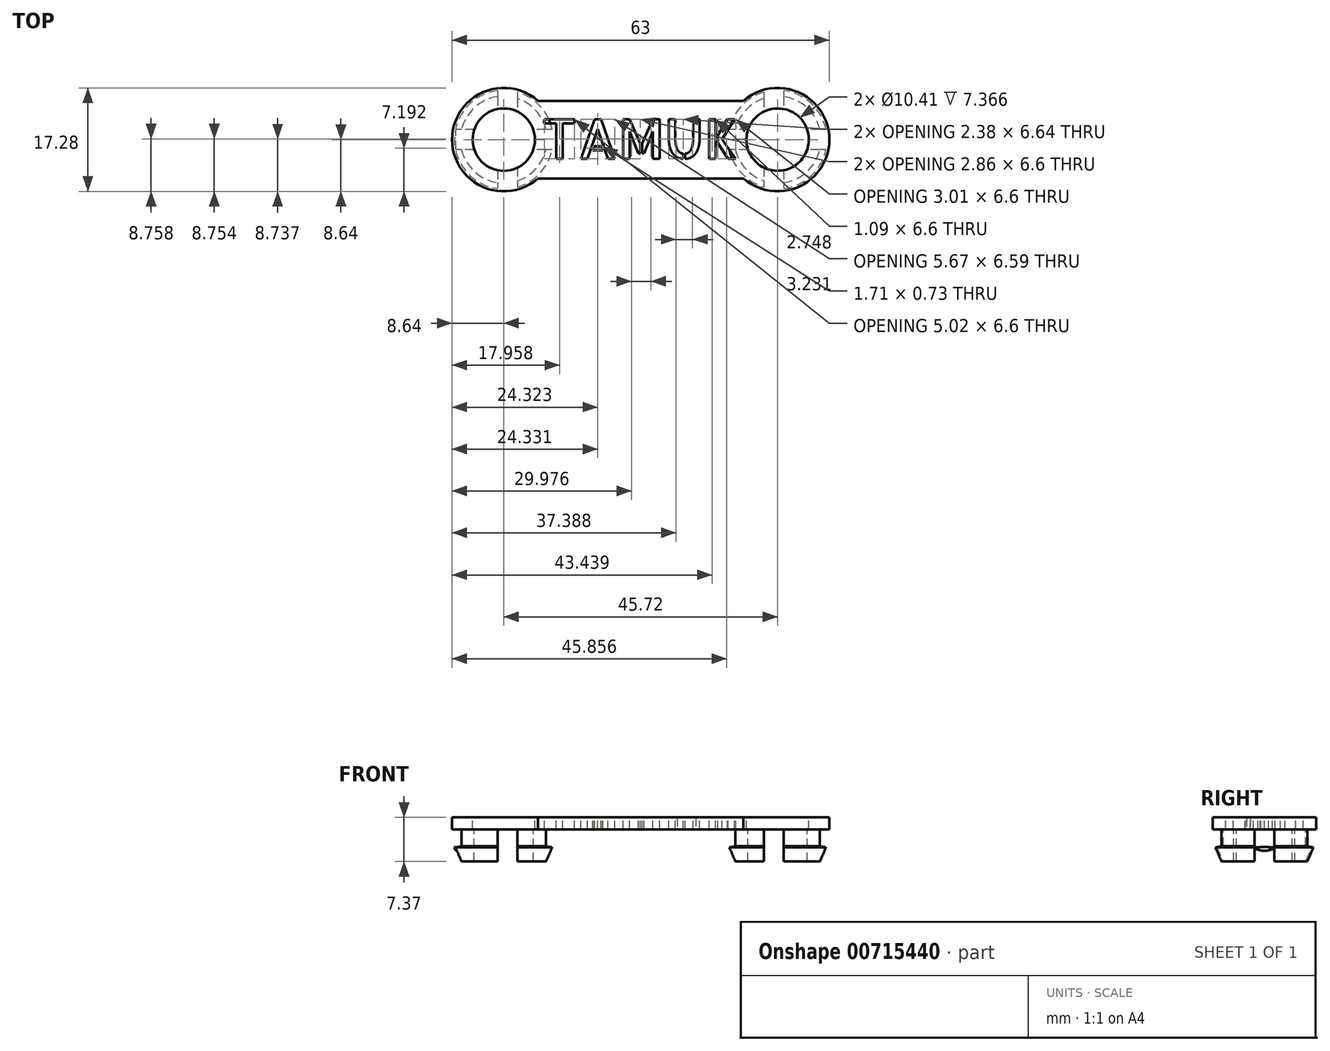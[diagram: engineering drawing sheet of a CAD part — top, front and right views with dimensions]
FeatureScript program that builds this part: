
annotation { "Feature Type Name" : "Feature", "Feature Type Description" : "" }
export const myFeature = defineFeature(function(context is Context, id is Id, definition is map)
    precondition{}
    {
        {
            var Q0;
            Q0=qCreatedBy(makeId("Top.planeOp"),FACE);
            var sketch = newSketch(context, id + "F0", { "sketchPlane" : qUnion([Q0])});
            skLineSegment(sketch, "E0", {"start": v(-17.15, -6.48) * mm, "end": v(17.15, -6.48) * mm});
            skLineSegment(sketch, "E1", {"start": v(-17.15, 6.48) * mm, "end": v(17.15, 6.48) * mm});
            skPoint(sketch, "E2", {"position": v(0, 6.48) * mm});
            skArc(sketch, "E3", {"start": v(-17.15, 6.48) * mm, "mid": v(-31.5, 0) * mm, "end": v(-17.15, -6.48) * mm});
            skArc(sketch, "E4", {"start": v(17.15, -6.48) * mm, "mid": v(31.5, 0) * mm, "end": v(17.15, 6.48) * mm});
            skSolve(sketch);
        }
        {
            var Q0;
            Q0=qCreatedBy(makeId("Front.planeOp"),FACE);
            var sketch = newSketch(context, id + "F1", { "sketchPlane" : qUnion([Q0])});
            skLineSegment(sketch, "E5", {"start": v(-28.07, 7.37) * mm, "end": v(-30.1, 7.37) * mm});
            skLineSegment(sketch, "E6", {"start": v(-30.1, 7.37) * mm, "end": v(-30.1, 7.37) * mm});
            skLineSegment(sketch, "E7", {"start": v(-30.1, 7.37) * mm, "end": v(-31.1, 5) * mm});
            skLineSegment(sketch, "E8", {"start": v(-31.1, 5) * mm, "end": v(-30.1, 4.83) * mm});
            skLineSegment(sketch, "E9", {"start": v(-22.86, 2.03) * mm, "end": v(-22.86, 0) * mm});
            skLineSegment(sketch, "E10", {"start": v(-28.07, 7.37) * mm, "end": v(-28.07, 2.03) * mm});
            skLineSegment(sketch, "E11", {"start": v(-30.1, 4.83) * mm, "end": v(-30.1, 2.03) * mm});
            skLineSegment(sketch, "E12", {"start": v(-28.07, 2.03) * mm, "end": v(-30.1, 2.03) * mm});
            skLineSegment(sketch, "E13", {"start": v(-22.86, 2.03) * mm, "end": v(-30.1, 2.03) * mm});
            skLineSegment(sketch, "E14.MirrorCS", {"start": v(-30.1, -7.37) * mm, "end": v(-31.1, -5) * mm});
            skLineSegment(sketch, "E15.MirrorCS", {"start": v(-30.1, -7.37) * mm, "end": v(-30.1, -7.37) * mm});
            skLineSegment(sketch, "E16.MirrorCS", {"start": v(-28.07, -7.37) * mm, "end": v(-30.1, -7.37) * mm});
            skLineSegment(sketch, "E17.MirrorCS", {"start": v(-28.07, -7.37) * mm, "end": v(-28.07, -2.03) * mm});
            skLineSegment(sketch, "E18.MirrorCS", {"start": v(-30.1, -4.83) * mm, "end": v(-30.1, -2.03) * mm});
            skLineSegment(sketch, "E19.MirrorCS", {"start": v(-22.86, -2.03) * mm, "end": v(-30.1, -2.03) * mm});
            skLineSegment(sketch, "E20.MirrorCS", {"start": v(-31.1, -5) * mm, "end": v(-30.1, -4.83) * mm});
            skSolve(sketch);
        }
        {
            var Q0;
            Q0=makeQuery(id+"F0.imprint","IMPRINT",FACE,{"disambiguationData":[TD([[makeQuery(id+"F0.imprint","IMPRINT",EDGE,{"derivedFrom":sQuery(id+"F0.wireOp",EDGE,"E0")}),1.0]])]});
            extrude(context, id + "F2", {"entities" : qUnion([Q0]), "oppositeDirection" : true, "depth" : 2.03 * mm, "offsetDistance" : 25.4 * mm});
        }
        {
            var Q0;
            Q0=makeQuery(id+"F1.imprint","IMPRINT",FACE,{"disambiguationData":[TD([[makeQuery(id+"F1.imprint","IMPRINT",EDGE,{"derivedFrom":sQuery(id+"F1.wireOp",EDGE,"E14.MirrorCS")}),-1.0]])]});
            var Q1;
            Q1=sQuery(id+"F1.wireOp",EDGE,"E9");
            revolve(context, id + "F3", {"operationType" : NewBodyOperationType.ADD, "surfaceOperationType" : NewSurfaceOperationType.NEW, "entities" : qUnion([Q0]), "axis" : qUnion([Q1]), "revolveType" : RevolveType.FULL});
        }
        {
            var Q0;
            Q0=makeQuery(id+"F2.opExtrude","SWEPT_BODY",BODY,{"disambiguationData":[OSD([sQuery(id+"F0.wireOp",EDGE,"E0"),sQuery(id+"F0.wireOp",EDGE,"E1"),sQuery(id+"F0.wireOp",EDGE,"E3"),sQuery(id+"F0.wireOp",EDGE,"E4")])]});
            var Q1;
            Q1=qCreatedBy(makeId("Right.planeOp"),FACE);
            mirror(context, id + "F4", {"operationType" : NewBodyOperationType.ADD, "entities" : qUnion([Q0]), "mirrorPlane" : qUnion([Q1])});
        }
        {
            var Q0;
            {var subQ0=sQuery(id+"F0.wireOp",EDGE,"E3");var subQ1=sQuery(id+"F0.wireOp",EDGE,"E1");var subQ2=sQuery(id+"F0.wireOp",EDGE,"E4");var subQ3=sQuery(id+"F0.wireOp",EDGE,"E0");Q0=makeQuery(id+"F4.boolean.opBoolean","SPLIT",FACE,{"disambiguationData":[TD([makeQuery(id+"F4.opPattern","COPY",FACE,{"derivedFrom":makeQuery(id+"F3.opRevolve","SWEPT_FACE",FACE,{"disambiguationData":[OSD([sQuery(id+"F1.wireOp",EDGE,"E17.MirrorCS")])]}),"instanceName":"1"})])],"derivedFrom":makeQuery(id+"F3.boolean.opBoolean","SPLIT",FACE,{"disambiguationData":[TD([makeQuery(id+"F2.opExtrude","SWEPT_FACE",FACE,{"disambiguationData":[OSD([subQ3])]})])],"derivedFrom":makeQuery(id+"F2.opExtrude","CAP_FACE",FACE,{"disambiguationData":[OSD([subQ3,subQ1,subQ0,subQ2])],"isStart":false})})});}
            var Q1;
            Q1=makeQuery(id+"F3.boolean.opBoolean","SPLIT",FACE,{"disambiguationData":[TD([makeQuery(id+"F3.opRevolve","SWEPT_FACE",FACE,{"disambiguationData":[OSD([sQuery(id+"F1.wireOp",EDGE,"E17.MirrorCS")])]})])],"derivedFrom":makeQuery(id+"F2.opExtrude","CAP_FACE",FACE,{"disambiguationData":[OSD([sQuery(id+"F0.wireOp",EDGE,"E0"),sQuery(id+"F0.wireOp",EDGE,"E1"),sQuery(id+"F0.wireOp",EDGE,"E3"),sQuery(id+"F0.wireOp",EDGE,"E4")])],"isStart":false})});
            extrude(context, id + "F5", {"entities" : qUnion([Q0, Q1]), "operationType" : NewBodyOperationType.REMOVE, "oppositeDirection" : true, "depth" : 25.4 * mm, "offsetDistance" : 25.4 * mm});
        }
        {
            var Q0;
            Q0=makeQuery(id+"F2.opExtrude","CAP_FACE",FACE,{"disambiguationData":[OSD([sQuery(id+"F0.wireOp",EDGE,"E0"),sQuery(id+"F0.wireOp",EDGE,"E1"),sQuery(id+"F0.wireOp",EDGE,"E3"),sQuery(id+"F0.wireOp",EDGE,"E4")])],"isStart":true});
            var sketch = newSketch(context, id + "F6", { "sketchPlane" : qUnion([Q0])});
            skText(sketch, "E21", { "text": "TAMUK", "fontName": "AllertaStencil-Regular.ttf"});
            const initialGuessF6  = {"E21": [-0.01651, -0.00318, 1, 0, 0.0066]};
            skSetInitialGuess(sketch, initialGuessF6);
            skSolve(sketch);
        }
        {
            var Q0;
            Q0=makeQuery(id+"F6.imprint","IMPRINT",FACE,{"disambiguationData":[TD([[makeQuery(id+"F6.imprint","IMPRINT",EDGE,{"derivedFrom":sQuery(id+"F6.wireOp",EDGE,"E21.sketch_text.stroke-0")}),-1.0]])]});
            var Q1;
            Q1=makeQuery(id+"F6.imprint","IMPRINT",FACE,{"disambiguationData":[TD([[makeQuery(id+"F6.imprint","IMPRINT",EDGE,{"derivedFrom":sQuery(id+"F6.wireOp",EDGE,"E21.sketch_text.stroke-8")}),-1.0]])]});
            var Q2;
            Q2=makeQuery(id+"F6.imprint","IMPRINT",FACE,{"disambiguationData":[TD([[makeQuery(id+"F6.imprint","IMPRINT",EDGE,{"derivedFrom":sQuery(id+"F6.wireOp",EDGE,"E21.sketch_text.stroke-15")}),-1.0]])]});
            var Q3;
            Q3=makeQuery(id+"F6.imprint","IMPRINT",FACE,{"disambiguationData":[TD([[makeQuery(id+"F6.imprint","IMPRINT",EDGE,{"derivedFrom":sQuery(id+"F6.wireOp",EDGE,"E21.sketch_text.stroke-19")}),-1.0]])]});
            var Q4;
            Q4=makeQuery(id+"F6.imprint","IMPRINT",FACE,{"disambiguationData":[TD([[makeQuery(id+"F6.imprint","IMPRINT",EDGE,{"derivedFrom":sQuery(id+"F6.wireOp",EDGE,"E21.sketch_text.stroke-27")}),-1.0]])]});
            var Q5;
            Q5=makeQuery(id+"F6.imprint","IMPRINT",FACE,{"disambiguationData":[TD([[makeQuery(id+"F6.imprint","IMPRINT",EDGE,{"derivedFrom":sQuery(id+"F6.wireOp",EDGE,"E21.sketch_text.stroke-35")}),-1.0]])]});
            var Q6;
            Q6=makeQuery(id+"F6.imprint","IMPRINT",FACE,{"disambiguationData":[TD([[makeQuery(id+"F6.imprint","IMPRINT",EDGE,{"derivedFrom":sQuery(id+"F6.wireOp",EDGE,"E21.sketch_text.stroke-47")}),-1.0]])]});
            var Q7;
            Q7=makeQuery(id+"F6.imprint","IMPRINT",FACE,{"disambiguationData":[TD([[makeQuery(id+"F6.imprint","IMPRINT",EDGE,{"derivedFrom":sQuery(id+"F6.wireOp",EDGE,"E21.sketch_text.stroke-59")}),-1.0]])]});
            var Q8;
            Q8=makeQuery(id+"F6.imprint","IMPRINT",FACE,{"disambiguationData":[TD([[makeQuery(id+"F6.imprint","IMPRINT",EDGE,{"derivedFrom":sQuery(id+"F6.wireOp",EDGE,"E21.sketch_text.stroke-63")}),-1.0]])]});
            extrude(context, id + "F7", {"entities" : qUnion([Q0, Q1, Q2, Q3, Q4, Q5, Q6, Q7, Q8]), "operationType" : NewBodyOperationType.REMOVE, "oppositeDirection" : true, "depth" : 2.54 * mm, "offsetDistance" : 25.4 * mm});
        }
        {
            var Q0;
            Q0=makeQuery(id+"F3.opRevolve","SWEPT_FACE",FACE,{"disambiguationData":[OSD([sQuery(id+"F1.wireOp",EDGE,"E16.MirrorCS")])]});
            var sketch = newSketch(context, id + "F8", { "sketchPlane" : qUnion([Q0])});
            skLineSegment(sketch, "E22.bottom", {"start": v(-23.89, -8.24) * mm, "end": v(-20.56, -8.24) * mm});
            skLineSegment(sketch, "E22.top", {"start": v(-23.89, 8.24) * mm, "end": v(-20.56, 8.24) * mm});
            skLineSegment(sketch, "E22.left", {"start": v(-23.89, -8.24) * mm, "end": v(-23.89, -1.66) * mm});
            skLineSegment(sketch, "E22.right", {"start": v(-20.56, -8.24) * mm, "end": v(-20.56, -1.66) * mm});
            skPoint(sketch, "E23", {"position": v(-22.23, 8.24) * mm});
            skLineSegment(sketch, "E24.MirrorCS", {"start": v(20.56, -8.24) * mm, "end": v(20.56, -1.66) * mm});
            skLineSegment(sketch, "E25.MirrorCS", {"start": v(23.89, 8.24) * mm, "end": v(20.56, 8.24) * mm});
            skLineSegment(sketch, "E26.MirrorCS", {"start": v(23.89, -8.24) * mm, "end": v(23.89, -1.66) * mm});
            skLineSegment(sketch, "E27.MirrorCS", {"start": v(23.89, -8.24) * mm, "end": v(20.56, -8.24) * mm});
            skLineSegment(sketch, "E28.bottom", {"start": v(-13.59, 1.66) * mm, "end": v(-20.56, 1.66) * mm});
            skLineSegment(sketch, "E28.top", {"start": v(-13.59, -1.66) * mm, "end": v(-20.56, -1.66) * mm});
            skLineSegment(sketch, "E28.left", {"start": v(-13.59, 1.66) * mm, "end": v(-13.59, -1.66) * mm});
            skLineSegment(sketch, "E28.right", {"start": v(-30.86, 1.66) * mm, "end": v(-30.86, -1.66) * mm});
            skPoint(sketch, "E28.middle", {"position": v(-22.23, 0) * mm});
            skLineSegment(sketch, "E29.bottom", {"start": v(31.34, 1.66) * mm, "end": v(23.89, 1.66) * mm});
            skLineSegment(sketch, "E29.top", {"start": v(31.34, -1.66) * mm, "end": v(23.89, -1.66) * mm});
            skLineSegment(sketch, "E29.left", {"start": v(31.34, 1.66) * mm, "end": v(31.34, -1.66) * mm});
            skLineSegment(sketch, "E29.right", {"start": v(13.1, 1.66) * mm, "end": v(13.1, -1.66) * mm});
            skPoint(sketch, "E29.middle", {"position": v(22.23, 0) * mm});
            skPoint(sketch, "E29.middle.positionSnap0", {"position": v(22.23, 8.24) * mm});
            skPoint(sketch, "E29.middle.positionSnap1", {"position": v(20.56, 0) * mm});
            skPoint(sketch, "E29.centerSnap0", {"position": v(22.23, 8.24) * mm});
            skPoint(sketch, "E29.centerSnap1", {"position": v(20.56, 0) * mm});
            skLineSegment(sketch, "E30.trimOffspring", {"start": v(-23.89, 1.66) * mm, "end": v(-30.86, 1.66) * mm});
            skLineSegment(sketch, "E31.trimOffspring", {"start": v(-20.56, 1.66) * mm, "end": v(-20.56, 8.24) * mm});
            skLineSegment(sketch, "E32.trimOffspring", {"start": v(-23.89, -1.66) * mm, "end": v(-30.86, -1.66) * mm});
            skLineSegment(sketch, "E33.trimOffspring", {"start": v(-23.89, 1.66) * mm, "end": v(-23.89, 8.24) * mm});
            skLineSegment(sketch, "E34.trimOffspring", {"start": v(20.56, 1.66) * mm, "end": v(13.1, 1.66) * mm});
            skLineSegment(sketch, "E35.trimOffspring", {"start": v(23.89, 1.66) * mm, "end": v(23.89, 8.24) * mm});
            skLineSegment(sketch, "E36.trimOffspring", {"start": v(20.56, -1.66) * mm, "end": v(13.1, -1.66) * mm});
            skLineSegment(sketch, "E37.trimOffspring", {"start": v(20.56, 1.66) * mm, "end": v(20.56, 8.24) * mm});
            skSolve(sketch);
        }
        {
            var Q0;
            {var subQ0=sQuery(id+"F8.wireOp",EDGE,"E22.bottom");Q0=makeQuery(id+"F8.imprint","IMPRINT",FACE,{"disambiguationData":[TD([[makeQuery(id+"F8.imprint","IMPRINT",EDGE,{"derivedFrom":subQ0}),1.0]])]});}
            var Q1;
            {var subQ0=sQuery(id+"F8.wireOp",EDGE,"E22.bottom");Q1=makeQuery(id+"F8.imprint","IMPRINT",FACE,{"disambiguationData":[TD([[makeQuery(id+"F8.imprint","IMPRINT",EDGE,{"derivedFrom":subQ0}),1.0]])]});}
            var Q2;
            {var subQ0=sQuery(id+"F8.wireOp",EDGE,"E22.top");Q2=makeQuery(id+"F8.imprint","IMPRINT",FACE,{"disambiguationData":[TD([[makeQuery(id+"F8.imprint","IMPRINT",EDGE,{"derivedFrom":subQ0}),-1.0]])]});}
            var Q3;
            {var subQ5=sQuery(id+"F8.wireOp",EDGE,"E32.trimOffspring");var subQ6=sQuery(id+"F8.wireOp",EDGE,"E22.left");var subQ7=makeQuery(id+"F8.imprint","INTERSECT",VERTEX,{"derivedFrom":[subQ6,subQ5]});Q3=makeQuery(id+"F8.imprint","IMPRINT",FACE,{"disambiguationData":[TD([[makeQuery(id+"F8.imprint","IMPRINT",EDGE,{"disambiguationData":[TD([[subQ7,1.0]])],"derivedFrom":subQ6}),-1.0]])]});}
            var Q4;
            Q4=makeQuery(id+"F8.imprint","IMPRINT",FACE,{"disambiguationData":[TD([[makeQuery(id+"F8.imprint","IMPRINT",EDGE,{"derivedFrom":sQuery(id+"F8.wireOp",EDGE,"E24.MirrorCS")}),-1.0]])]});
            var Q5;
            {var subQ0=sQuery(id+"F8.wireOp",EDGE,"E28.bottom");var subQ1=sQuery(id+"F1.wireOp",EDGE,"E16.MirrorCS");var subQ2=makeQuery(id+"F3.opRevolve","SWEPT_EDGE",EDGE,{"disambiguationData":[OSD([sQuery(id+"F1.wireOp",EDGE,"E14.MirrorCS"),subQ1])]});var subQ3=makeQuery(id+"F8.imprint","INTERSECT",VERTEX,{"derivedFrom":[subQ2,subQ0]});Q5=makeQuery(id+"F8.imprint","IMPRINT",FACE,{"disambiguationData":[TD([[makeQuery(id+"F8.imprint","IMPRINT",EDGE,{"disambiguationData":[TD([[subQ3,-1.0]])],"derivedFrom":subQ0}),1.0]])]});}
            var Q6;
            {var subQ0=sQuery(id+"F8.wireOp",EDGE,"E28.left");Q6=makeQuery(id+"F8.imprint","IMPRINT",FACE,{"disambiguationData":[TD([[makeQuery(id+"F8.imprint","IMPRINT",EDGE,{"derivedFrom":subQ0}),-1.0]])]});}
            var Q7;
            {var subQ0=sQuery(id+"F8.wireOp",EDGE,"E31.trimOffspring");var subQ1=sQuery(id+"F1.wireOp",EDGE,"E16.MirrorCS");var subQ2=makeQuery(id+"F3.opRevolve","SWEPT_EDGE",EDGE,{"disambiguationData":[OSD([sQuery(id+"F1.wireOp",EDGE,"E14.MirrorCS"),subQ1])]});var subQ3=makeQuery(id+"F8.imprint","INTERSECT",VERTEX,{"derivedFrom":[subQ2,subQ0]});Q7=makeQuery(id+"F8.imprint","IMPRINT",FACE,{"disambiguationData":[TD([[makeQuery(id+"F8.imprint","IMPRINT",EDGE,{"disambiguationData":[TD([[subQ3,1.0]])],"derivedFrom":subQ0}),1.0]])]});}
            var Q8;
            {var subQ0=sQuery(id+"F8.wireOp",EDGE,"E30.trimOffspring");var subQ1=sQuery(id+"F1.wireOp",EDGE,"E16.MirrorCS");var subQ2=makeQuery(id+"F3.opRevolve","SWEPT_EDGE",EDGE,{"disambiguationData":[OSD([sQuery(id+"F1.wireOp",EDGE,"E14.MirrorCS"),subQ1])]});var subQ3=makeQuery(id+"F8.imprint","INTERSECT",VERTEX,{"derivedFrom":[subQ2,subQ0]});Q8=makeQuery(id+"F8.imprint","IMPRINT",FACE,{"disambiguationData":[TD([[makeQuery(id+"F8.imprint","IMPRINT",EDGE,{"disambiguationData":[TD([[subQ3,1.0]])],"derivedFrom":subQ0}),1.0]])]});}
            var Q9;
            {var subQ0=sQuery(id+"F8.wireOp",EDGE,"E28.right");Q9=makeQuery(id+"F8.imprint","IMPRINT",FACE,{"disambiguationData":[TD([[makeQuery(id+"F8.imprint","IMPRINT",EDGE,{"derivedFrom":subQ0}),1.0]])]});}
            var Q10;
            {var subQ0=sQuery(id+"F8.wireOp",EDGE,"E22.left");var subQ1=sQuery(id+"F1.wireOp",EDGE,"E16.MirrorCS");var subQ2=makeQuery(id+"F3.opRevolve","SWEPT_EDGE",EDGE,{"disambiguationData":[OSD([sQuery(id+"F1.wireOp",EDGE,"E14.MirrorCS"),subQ1])]});var subQ3=makeQuery(id+"F8.imprint","INTERSECT",VERTEX,{"derivedFrom":[subQ2,subQ0]});Q10=makeQuery(id+"F8.imprint","IMPRINT",FACE,{"disambiguationData":[TD([[makeQuery(id+"F8.imprint","IMPRINT",EDGE,{"disambiguationData":[TD([[subQ3,-1.0]])],"derivedFrom":subQ0}),-1.0]])]});}
            var Q11;
            {var subQ0=sQuery(id+"F0.wireOp",EDGE,"E3");var subQ2=sQuery(id+"F0.wireOp",EDGE,"E1");var subQ4=sQuery(id+"F0.wireOp",EDGE,"E4");var subQ6=sQuery(id+"F0.wireOp",EDGE,"E0");var subQ7=makeQuery(id+"F2.opExtrude","SWEPT_FACE",FACE,{"disambiguationData":[OSD([subQ6])]});Q11=makeQuery(id+"F4.boolean.opBoolean","SPLIT",FACE,{"disambiguationData":[TD([subQ7])],"derivedFrom":makeQuery(id+"F3.boolean.opBoolean","SPLIT",FACE,{"disambiguationData":[TD([subQ7])],"derivedFrom":makeQuery(id+"F2.opExtrude","CAP_FACE",FACE,{"disambiguationData":[OSD([subQ6,subQ2,subQ0,subQ4])],"isStart":false})})});}
            extrude(context, id + "F9", {"entities" : qUnion([Q0, Q1, Q2, Q3, Q4, Q5, Q6, Q7, Q8, Q9, Q10]), "operationType" : NewBodyOperationType.REMOVE, "endBound" : BoundingType.UP_TO_SURFACE, "oppositeDirection" : true, "depth" : 25.4 * mm, "endBoundEntityFace" : qUnion([Q11]), "offsetDistance" : 25.4 * mm});
        }
    });
